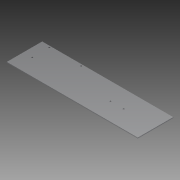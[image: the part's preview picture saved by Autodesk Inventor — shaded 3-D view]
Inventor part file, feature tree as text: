
AUTODESK INVENTOR PART (.ipt)
format: ipt  version: 2013 (Build 170138000, 138)  size: 84,992 bytes
history: native  units: in
note: dims shown in document units (in); Inventor stores cm internally (conversion verified against a paired STEP export)
features: extrude x1, sketch x1
ambient origin geometry x8: Origin, YZ Plane, XZ Plane, XY Plane, X Axis, Y Axis, Z Axis, Center Point
bodies: Solid1 (feature_tree)
feature tree (2):
  extrude  "Extrusion1"  Depth=5.0in
  sketch  "Sketch1"  dims[d0=18.5in d2=5.0in d3=0.2in d4=4.5in d5=2.4in d6=1.25in d7=0.25in d8=1.86in d9=0.2in d10=2.5in d11=4.5in d12=0.125in d13=0.0in]
